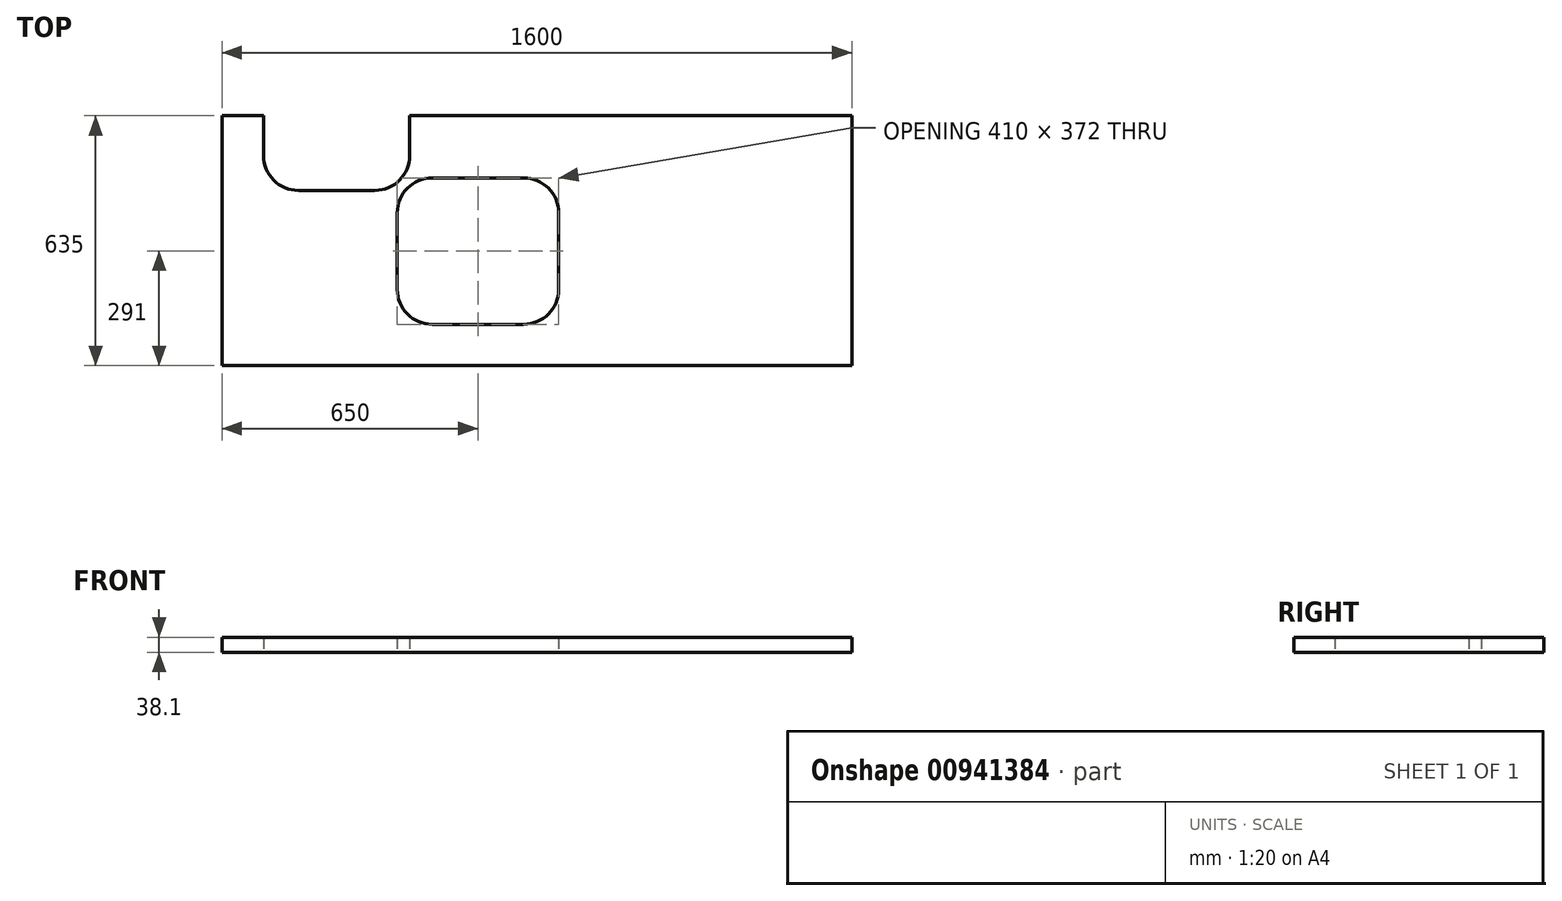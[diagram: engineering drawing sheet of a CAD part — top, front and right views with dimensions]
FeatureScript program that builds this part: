
annotation { "Feature Type Name" : "Feature", "Feature Type Description" : "" }
export const myFeature = defineFeature(function(context is Context, id is Id, definition is map)
    precondition{}
    {
        {
            var Q0;
            Q0=qCreatedBy(makeId("Right.planeOp"),FACE);
            var sketch = newSketch(context, id + "F0", { "sketchPlane" : qUnion([Q0])});
            skLineSegment(sketch, "E0.bottom", {"start": v(0, 0) * mm, "end": v(635, 0) * mm});
            skLineSegment(sketch, "E0.top", {"start": v(0, 38.1) * mm, "end": v(635, 38.1) * mm});
            skLineSegment(sketch, "E0.left", {"start": v(0, 0) * mm, "end": v(0, 38.1) * mm});
            skLineSegment(sketch, "E0.right", {"start": v(635, 0) * mm, "end": v(635, 38.1) * mm});
            skPoint(sketch, "E1.visualSharp", {"position": v(635, 38.1) * mm});
            skArc(sketch, "E1.filletArc", {"start": v(635, 19.05) * mm, "mid": v(629.42, 32.52) * mm, "end": v(615.95, 38.1) * mm, "construction": true});
            skSolve(sketch);
        }
        {
            var Q0;
            Q0=makeQuery(id+"F0.imprint","IMPRINT",FACE,{"disambiguationData":[TD([[makeQuery(id+"F0.imprint","IMPRINT",EDGE,{"derivedFrom":sQuery(id+"F0.wireOp",EDGE,"E0.bottom")}),1.0]])]});
            extrude(context, id + "F1", {"entities" : qUnion([Q0]), "depth" : 1600 * mm, "offsetDistance" : 25 * mm});
        }
        {
            var Q0;
            Q0=qCreatedBy(makeId("Top.planeOp"),FACE);
            var sketch = newSketch(context, id + "F2", { "sketchPlane" : qUnion([Q0])});
            skLineSegment(sketch, "E2.bottom", {"start": v(105, 635) * mm, "end": v(477, 635) * mm});
            skLineSegment(sketch, "E2.top", {"start": v(105, 445) * mm, "end": v(477, 445) * mm});
            skLineSegment(sketch, "E2.left", {"start": v(105, 635) * mm, "end": v(105, 445) * mm});
            skLineSegment(sketch, "E2.right", {"start": v(477, 635) * mm, "end": v(477, 445) * mm});
            skSolve(sketch);
        }
        {
            var Q0;
            Q0 = qSketchRegion(id + "F2", true);
            extrude(context, id + "F3", {"entities" : qUnion([Q0]), "operationType" : NewBodyOperationType.REMOVE, "endBound" : BoundingType.THROUGH_ALL, "depth" : 25 * mm, "offsetDistance" : 25 * mm});
        }
        {
            var Q0;
            Q0=makeQuery(id+"F3.boolean.opBoolean","COPY",EDGE,{"derivedFrom":makeQuery(id+"F3.opExtrude","SWEPT_EDGE",EDGE,{"disambiguationData":[OSD([sQuery(id+"F2.wireOp",EDGE,"E2.top"),sQuery(id+"F2.wireOp",EDGE,"E2.right")])]})});
            var Q1;
            Q1=makeQuery(id+"F3.boolean.opBoolean","COPY",EDGE,{"derivedFrom":makeQuery(id+"F3.opExtrude","SWEPT_EDGE",EDGE,{"disambiguationData":[OSD([sQuery(id+"F2.wireOp",EDGE,"E2.top"),sQuery(id+"F2.wireOp",EDGE,"E2.left")])]})});
            fillet(context, id + "F4", {"entities" : qUnion([Q0, Q1]), "radius" : 88.9 * mm, "tangentPropagation" : true, "allowEdgeOverflow" : false});
        }
        {
            var Q0;
            Q0=qCreatedBy(makeId("Top.planeOp"),FACE);
            var sketch = newSketch(context, id + "F5", { "sketchPlane" : qUnion([Q0])});
            skLineSegment(sketch, "E3.bottom", {"start": v(766.1, 105) * mm, "end": v(533.9, 105) * mm});
            skLineSegment(sketch, "E3.top", {"start": v(766.1, 477) * mm, "end": v(533.9, 477) * mm});
            skLineSegment(sketch, "E3.left", {"start": v(855, 193.9) * mm, "end": v(855, 388.1) * mm});
            skLineSegment(sketch, "E3.right", {"start": v(445, 193.9) * mm, "end": v(445, 388.1) * mm});
            skPoint(sketch, "E4.visualSharp", {"position": v(855, 105) * mm});
            skArc(sketch, "E4.filletArc", {"start": v(766.1, 105) * mm, "mid": v(828.96, 131.04) * mm, "end": v(855, 193.9) * mm});
            skPoint(sketch, "E5.visualSharp", {"position": v(855, 477) * mm});
            skArc(sketch, "E5.filletArc", {"start": v(855, 388.1) * mm, "mid": v(828.96, 450.96) * mm, "end": v(766.1, 477) * mm});
            skPoint(sketch, "E6.visualSharp", {"position": v(445, 477) * mm});
            skArc(sketch, "E6.filletArc", {"start": v(533.9, 477) * mm, "mid": v(471.04, 450.96) * mm, "end": v(445, 388.1) * mm});
            skPoint(sketch, "E7.visualSharp", {"position": v(445, 105) * mm});
            skArc(sketch, "E7.filletArc", {"start": v(445, 193.9) * mm, "mid": v(471.04, 131.04) * mm, "end": v(533.9, 105) * mm});
            skSolve(sketch);
        }
        {
            var Q0;
            Q0 = qSketchRegion(id + "F5", true);
            extrude(context, id + "F6", {"entities" : qUnion([Q0]), "operationType" : NewBodyOperationType.REMOVE, "endBound" : BoundingType.THROUGH_ALL, "depth" : 25 * mm, "offsetDistance" : 25 * mm});
        }
    });
